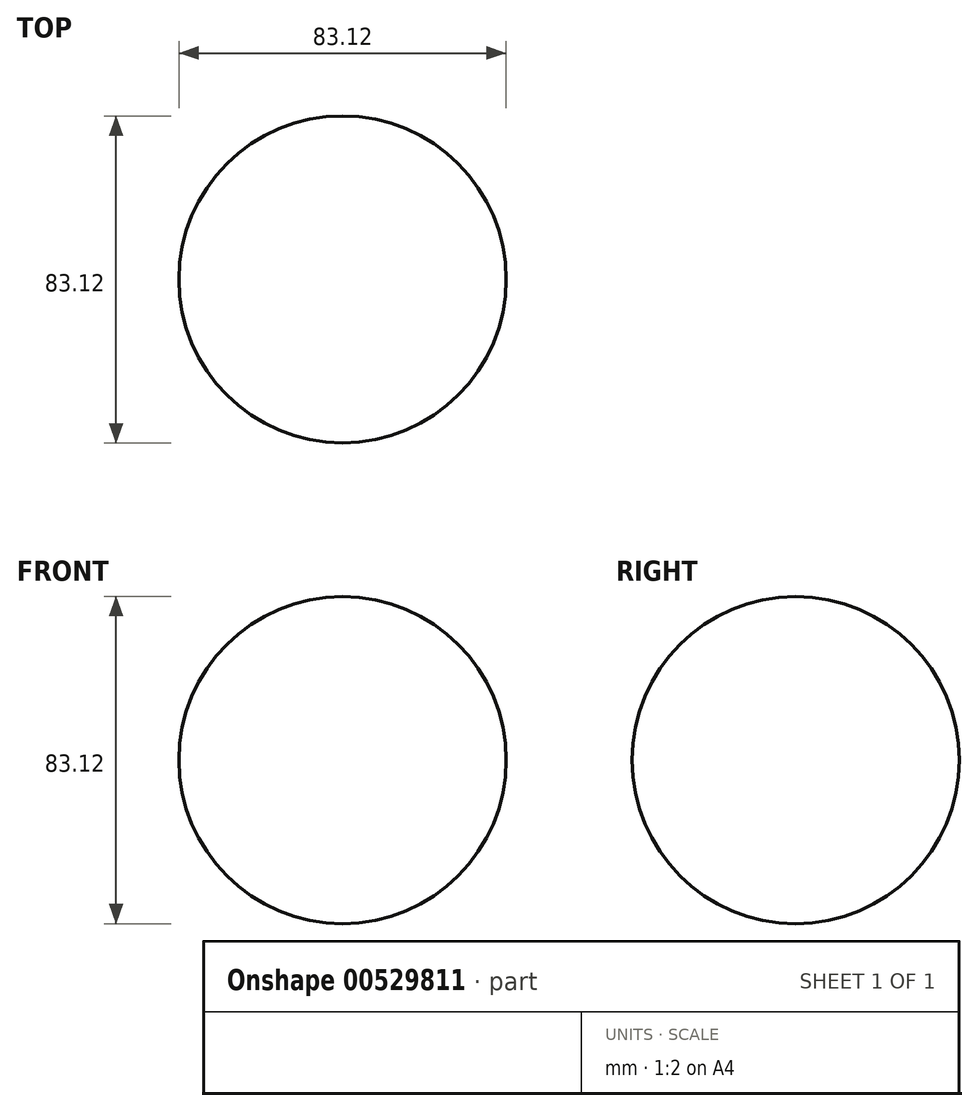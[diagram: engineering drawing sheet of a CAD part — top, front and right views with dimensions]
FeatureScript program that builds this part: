
annotation { "Feature Type Name" : "Feature", "Feature Type Description" : "" }
export const myFeature = defineFeature(function(context is Context, id is Id, definition is map)
    precondition{}
    {
        {
            var Q0;
            Q0=qCreatedBy(makeId("Top.planeOp"),FACE);
            var sketch = newSketch(context, id + "F0", { "sketchPlane" : qUnion([Q0])});
            skArc(sketch, "E0", {"start": v(41.56, 0) * mm, "mid": v(0, 41.56) * mm, "end": v(-41.56, 0) * mm});
            skLineSegment(sketch, "E1", {"start": v(-41.56, 0) * mm, "end": v(41.56, 0) * mm});
            skSolve(sketch);
        }
        {
            var Q0;
            Q0=makeQuery(id+"F0.imprint","IMPRINT",FACE,{"disambiguationData":[TD([[makeQuery(id+"F0.imprint","IMPRINT",EDGE,{"derivedFrom":sQuery(id+"F0.wireOp",EDGE,"E0")}),1.0]])]});
            var Q1;
            Q1=sQuery(id+"F0.wireOp",EDGE,"E1");
            revolve(context, id + "F1", {"entities" : qUnion([Q0]), "axis" : qUnion([Q1]), "revolveType" : RevolveType.FULL});
        }
    });
